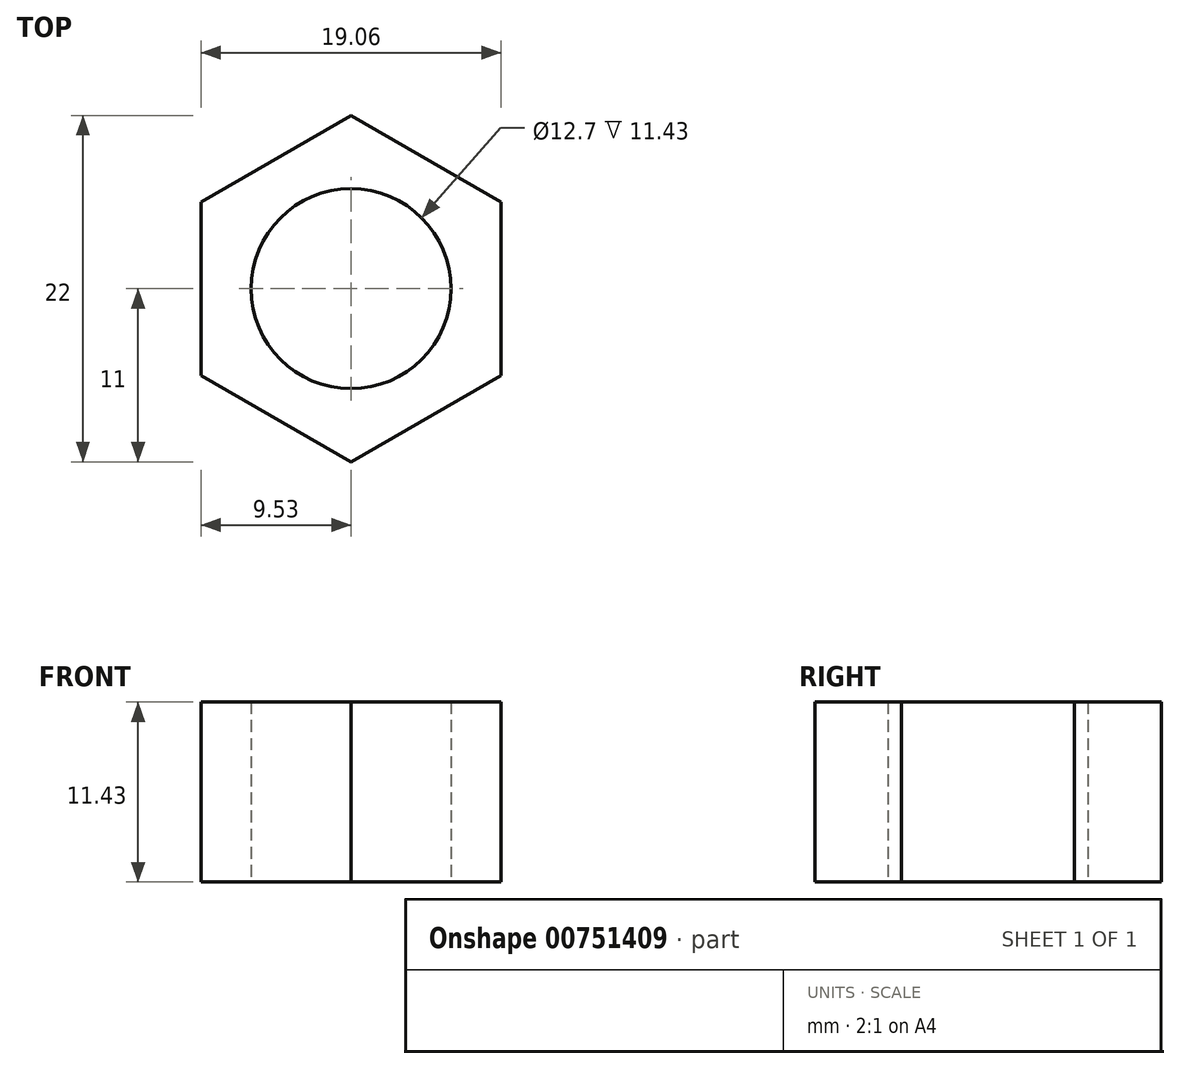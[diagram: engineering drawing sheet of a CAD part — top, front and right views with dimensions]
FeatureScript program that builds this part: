
annotation { "Feature Type Name" : "Feature", "Feature Type Description" : "" }
export const myFeature = defineFeature(function(context is Context, id is Id, definition is map)
    precondition{}
    {
        {
            var Q0;
            Q0=qCreatedBy(makeId("Top.planeOp"),FACE);
            var sketch = newSketch(context, id + "F0", { "sketchPlane" : qUnion([Q0])});
            skCircle(sketch, "E0.cCircle", {"center": v(0, 0) * mm, "radius": 9.53 * mm, "construction": true});
            skLineSegment(sketch, "E0.0", {"start": v(9.53, 5.5) * mm, "end": v(9.53, -5.5) * mm});
            skLineSegment(sketch, "E0.1", {"start": v(9.52, -5.5) * mm, "end": v(0, -11) * mm});
            skLineSegment(sketch, "E0.2", {"start": v(0, -11) * mm, "end": v(-9.52, -5.5) * mm});
            skLineSegment(sketch, "E0.3", {"start": v(-9.52, -5.5) * mm, "end": v(-9.53, 5.5) * mm});
            skLineSegment(sketch, "E0.4", {"start": v(-9.52, 5.5) * mm, "end": v(0, 11) * mm});
            skLineSegment(sketch, "E0.5", {"start": v(0, 11) * mm, "end": v(9.52, 5.5) * mm});
            skPoint(sketch, "E0.0.midPoint", {"position": v(9.53, 0) * mm});
            skCircle(sketch, "E1", {"center": v(0, 0) * mm, "radius": 6.35 * mm});
            skSolve(sketch);
        }
        {
            var Q0;
            Q0=makeQuery(id+"F0.imprint","IMPRINT",FACE,{"disambiguationData":[TD([[makeQuery(id+"F0.imprint","IMPRINT",EDGE,{"derivedFrom":sQuery(id+"F0.wireOp",EDGE,"E0.0")}),-1.0]])]});
            extrude(context, id + "F1", {"entities" : qUnion([Q0]), "depth" : 11.43 * mm, "offsetDistance" : 25.4 * mm});
        }
    });
